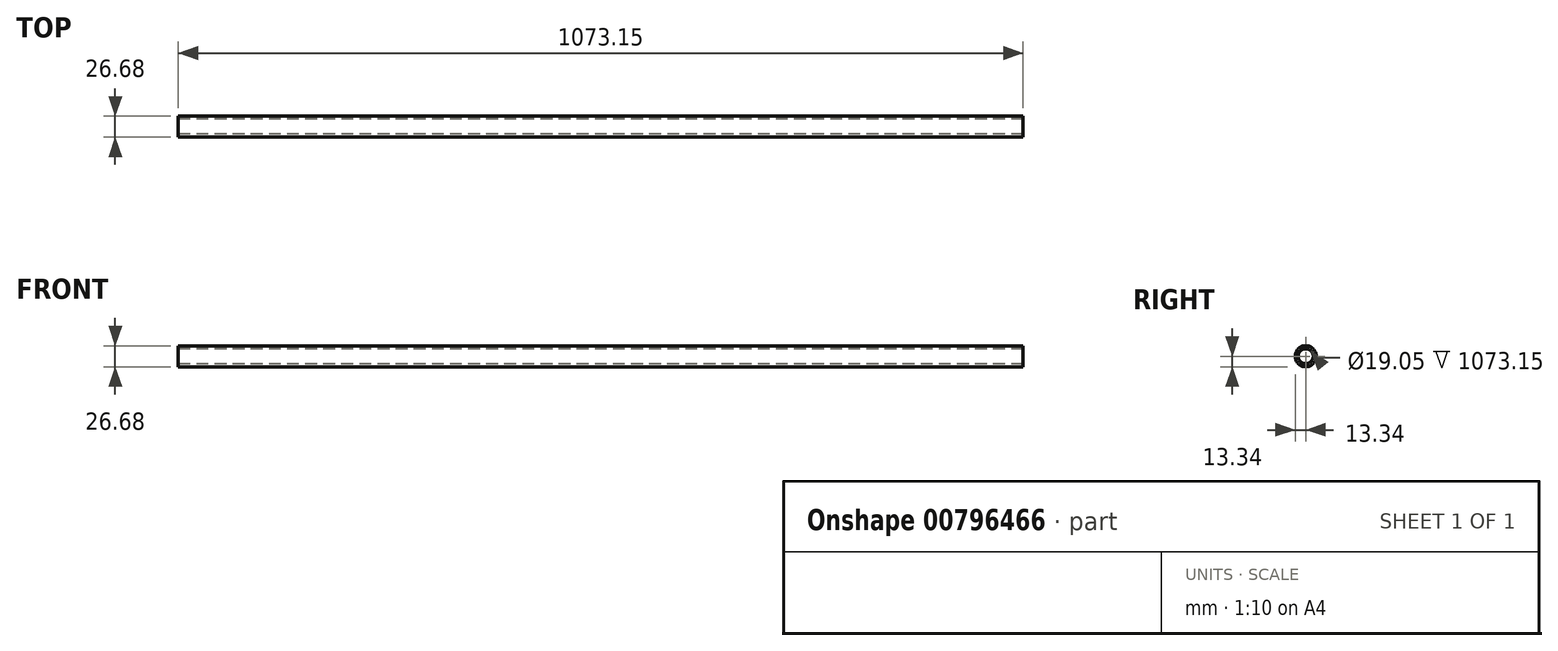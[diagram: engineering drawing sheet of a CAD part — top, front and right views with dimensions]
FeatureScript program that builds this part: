
annotation { "Feature Type Name" : "Feature", "Feature Type Description" : "" }
export const myFeature = defineFeature(function(context is Context, id is Id, definition is map)
    precondition{}
    {
        {
            var Q0;
            Q0=qCreatedBy(makeId("Right.planeOp"),FACE);
            var sketch = newSketch(context, id + "F0", { "sketchPlane" : qUnion([Q0])});
            skCircle(sketch, "E0", {"center": v(0, 0) * mm, "radius": 9.53 * mm});
            skCircle(sketch, "E1.0", {"center": v(0, 0) * mm, "radius": 13.33 * mm});
            skSolve(sketch);
        }
        {
            var Q0;
            Q0=qSketchRegion(id+"F0",true);
            extrude(context, id + "F1", {"entities" : qUnion([Q0]), "depth" : 1073.15 * mm, "offsetDistance" : 25.4 * mm});
        }
    });
